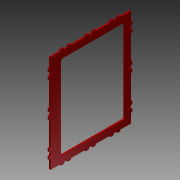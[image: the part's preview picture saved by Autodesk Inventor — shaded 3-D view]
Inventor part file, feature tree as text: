
AUTODESK INVENTOR PART (.ipt)
format: ipt  version: 2013 (Build 170138000, 138)  size: 484,864 bytes
history: native  units: mm
features: extrude x2, sketch x2
ambient origin geometry x8: Origin, YZ Plane, XZ Plane, XY Plane, X Axis, Y Axis, Z Axis, Center Point
feature tree (4):
  extrude  "Extrusion2"  Depth=70.072433mm
  extrude  "Extrusion3"  Depth=325.3mm
  sketch  "Sketch3"  dims[d59=51.38645mm d60=70.072433mm]
  sketch  "Sketch4"  dims[d63=395.2mm d64=325.3mm d65=6.0mm d66=6.0mm d67=6.0mm d68=6.0mm d69=7.0mm d70=1.8mm d71=1.8mm d72=3.0mm d73=1.25mm d74=1.25mm d76=12.4mm d77=6.1mm d78=11.8mm d79=0.3mm d80=6.1mm d81=12.4mm d82=100.0mm d83=6.1mm d84=12.4mm d85=3.0mm d86=6.1mm d87=12.4mm d88=1.25mm d89=1.25mm d90=100.0mm d91=6.1mm d92=12.4mm d93=6.1mm d94=12.4mm d95=3.0mm d96=1.25mm d97=1.25mm d98=10.6mm d99=1.8mm d100=1.8mm d101=28.0mm d102=42.0mm d103=24.0mm d104=28.0mm d105=10.0mm d106=6.0mm d107=0.0mm d108=7.9mm d109=3.0mm d110=11.0mm d111=11.0mm d112=78.5mm d113=78.5mm d114=22.0mm d115=10.6mm d116=1.8mm d117=1.8mm d119=6.1mm d120=12.4mm d121=3.0mm d122=1.25mm d123=1.25mm d124=6.1mm d125=12.4mm d126=140.0mm d127=6.1mm d128=12.4mm d129=3.0mm d130=6.1mm d131=12.4mm d132=1.25mm d133=1.25mm d134=140.0mm d135=6.1mm d136=12.4mm d137=3.0mm d138=6.1mm d139=12.4mm d140=1.25mm d141=1.25mm d142=7.0mm d143=1.8mm d144=1.8mm d145=11.0mm d146=11.0mm d147=199.1mm d148=161.15mm d151=6.2mm d153=1.5mm d154=10.0mm d155=0.0mm d156=1.8mm]
